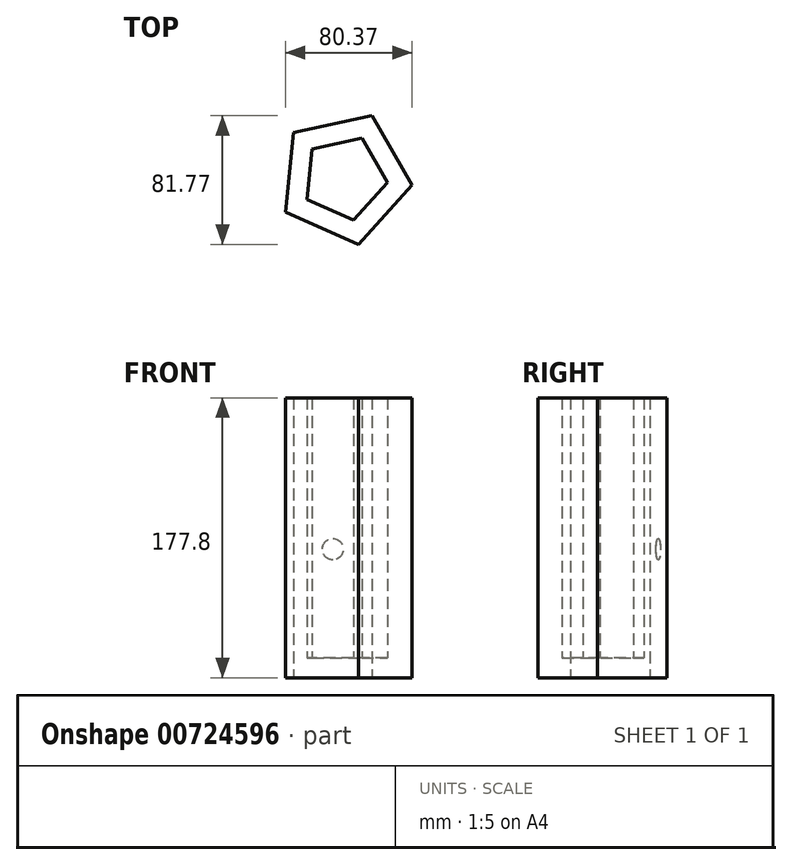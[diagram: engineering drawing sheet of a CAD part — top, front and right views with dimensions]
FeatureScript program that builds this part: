
annotation { "Feature Type Name" : "Feature", "Feature Type Description" : "" }
export const myFeature = defineFeature(function(context is Context, id is Id, definition is map)
    precondition{}
    {
        {
            var Q0;
            Q0=qCreatedBy(makeId("Top.planeOp"),FACE);
            var sketch = newSketch(context, id + "F0", { "sketchPlane" : qUnion([Q0])});
            skCircle(sketch, "E0.cCircle", {"center": v(0, 0) * mm, "radius": 34.96 * mm, "construction": true});
            skLineSegment(sketch, "E0.0", {"start": v(17.5, 39.52) * mm, "end": v(42.99, -4.42) * mm});
            skLineSegment(sketch, "E0.1", {"start": v(42.99, -4.42) * mm, "end": v(9.08, -42.25) * mm});
            skLineSegment(sketch, "E0.2", {"start": v(9.08, -42.25) * mm, "end": v(-37.38, -21.69) * mm});
            skLineSegment(sketch, "E0.3", {"start": v(-37.38, -21.69) * mm, "end": v(-32.18, 28.85) * mm});
            skLineSegment(sketch, "E0.4", {"start": v(-32.18, 28.85) * mm, "end": v(17.5, 39.52) * mm});
            skPoint(sketch, "E0.0.midPoint", {"position": v(30.24, 17.55) * mm});
            skSolve(sketch);
        }
        {
            var Q0;
            Q0 = qSketchRegion(id + "F0", true);
            extrude(context, id + "F1", {"entities" : qUnion([Q0]), "depth" : 177.8 * mm, "offsetDistance" : 25.4 * mm});
        }
        {
            var Q0;
            Q0=makeQuery(id+"F1.opExtrude","CAP_FACE",FACE,{"disambiguationData":[OSD([sQuery(id+"F0.wireOp",EDGE,"E0.0"),sQuery(id+"F0.wireOp",EDGE,"E0.1"),sQuery(id+"F0.wireOp",EDGE,"E0.2"),sQuery(id+"F0.wireOp",EDGE,"E0.3"),sQuery(id+"F0.wireOp",EDGE,"E0.4")])],"isStart":false});
            shell(context, id + "F2", {"entities" : qUnion([Q0]), "thickness" : 12.7 * mm});
        }
        {
            var Q0;
            Q0=makeQuery(id+"F1.opExtrude","SWEPT_FACE",FACE,{"disambiguationData":[OSD([sQuery(id+"F0.wireOp",EDGE,"E0.4")])]});
            var sketch = newSketch(context, id + "F3", { "sketchPlane" : qUnion([Q0])});
            skCircle(sketch, "E1", {"center": v(0, 81.71) * mm, "radius": 6.76 * mm});
            skSolve(sketch);
        }
        {
            var Q0;
            Q0 = qSketchRegion(id + "F3", true);
            extrude(context, id + "F4", {"entities" : qUnion([Q0]), "operationType" : NewBodyOperationType.REMOVE, "oppositeDirection" : true, "depth" : 0.08 * mm, "offsetDistance" : 25.4 * mm});
        }
    });
